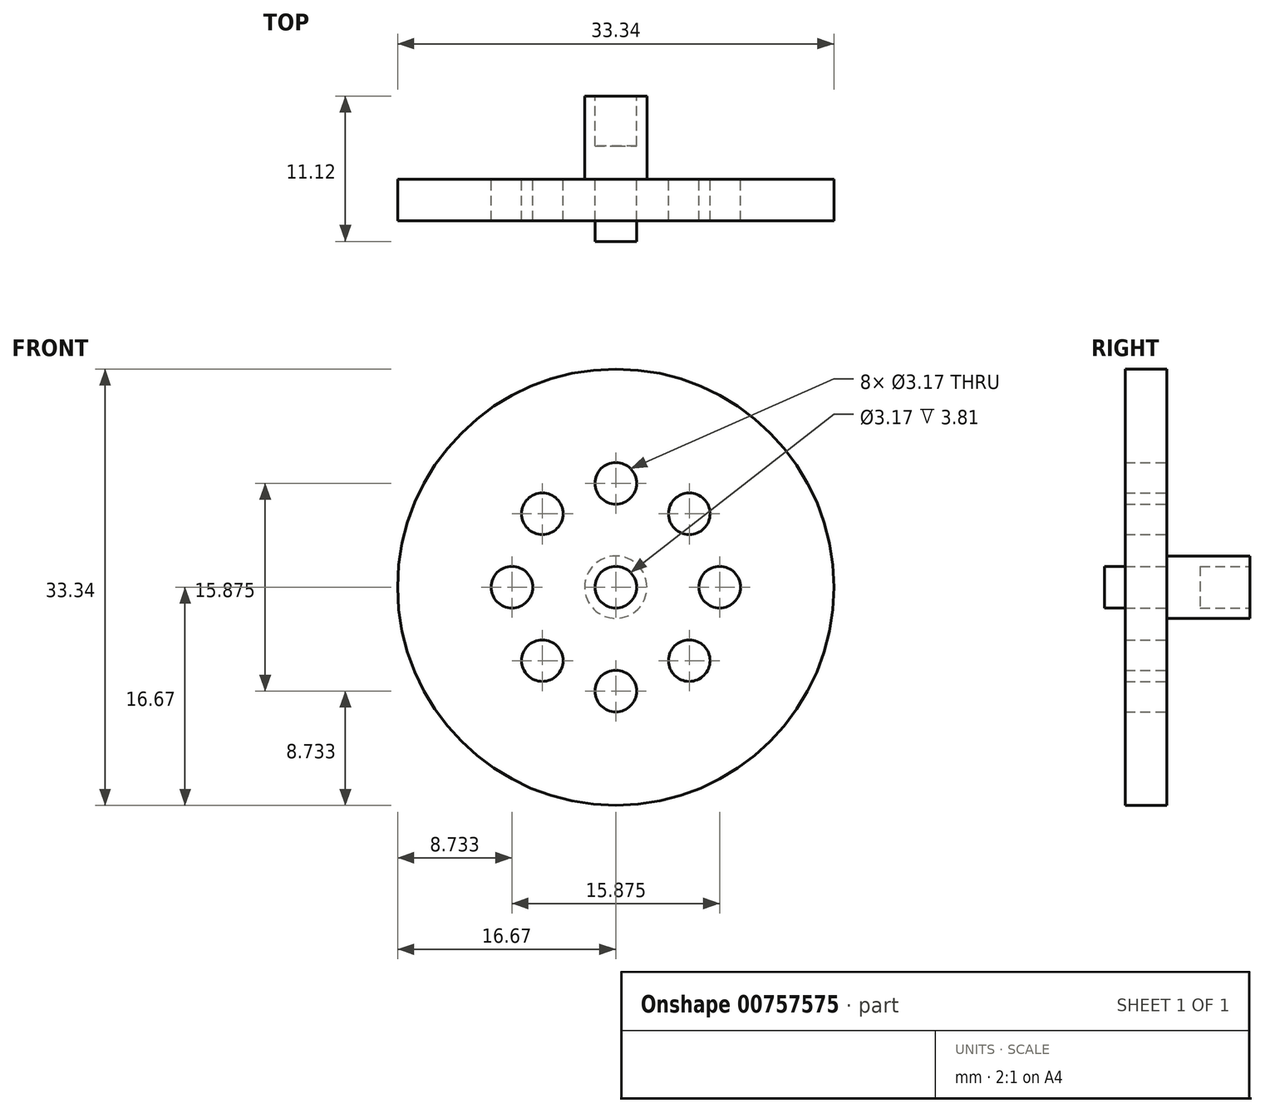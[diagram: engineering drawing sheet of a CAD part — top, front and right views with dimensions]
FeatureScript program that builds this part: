
annotation { "Feature Type Name" : "Feature", "Feature Type Description" : "" }
export const myFeature = defineFeature(function(context is Context, id is Id, definition is map)
    precondition{}
    {
        {
            var Q0;
            Q0=qCreatedBy(makeId("Front.planeOp"),FACE);
            var sketch = newSketch(context, id + "F0", { "sketchPlane" : qUnion([Q0])});
            skCircle(sketch, "E0", {"center": v(0, 0) * mm, "radius": 16.67 * mm});
            skSolve(sketch);
        }
        {
            var Q0;
            Q0=makeQuery(id+"F0.imprint","IMPRINT",FACE,{"disambiguationData":[TD([[makeQuery(id+"F0.imprint","IMPRINT",EDGE,{"derivedFrom":sQuery(id+"F0.wireOp",EDGE,"E0")}),1.0]])]});
            extrude(context, id + "F1", {"entities" : qUnion([Q0]), "oppositeDirection" : true, "depth" : 3.17 * mm, "offsetDistance" : 25.4 * mm});
        }
        {
            var Q0;
            Q0=makeQuery(id+"F1.opExtrude","CAP_FACE",FACE,{"disambiguationData":[OSD([sQuery(id+"F0.wireOp",EDGE,"E0")])],"isStart":false});
            var sketch = newSketch(context, id + "F2", { "sketchPlane" : qUnion([Q0])});
            skCircle(sketch, "E1", {"center": v(0, 0) * mm, "radius": 2.38 * mm});
            skSolve(sketch);
        }
        {
            var Q0;
            Q0=makeQuery(id+"F2.imprint","IMPRINT",FACE,{"disambiguationData":[TD([[makeQuery(id+"F2.imprint","IMPRINT",EDGE,{"derivedFrom":sQuery(id+"F2.wireOp",EDGE,"E1")}),1.0]])]});
            extrude(context, id + "F3", {"entities" : qUnion([Q0]), "operationType" : NewBodyOperationType.ADD, "depth" : 6.35 * mm, "offsetDistance" : 25.4 * mm});
        }
        {
            var Q0;
            Q0=makeQuery(id+"F3.opExtrude","CAP_FACE",FACE,{"disambiguationData":[OSD([sQuery(id+"F2.wireOp",EDGE,"E1")])],"isStart":false});
            var sketch = newSketch(context, id + "F4", { "sketchPlane" : qUnion([Q0])});
            skCircle(sketch, "E2", {"center": v(7.94, 0) * mm, "radius": 1.59 * mm});
            skCircle(sketch, "E3.1.0", {"center": v(5.61, 5.61) * mm, "radius": 1.59 * mm});
            skCircle(sketch, "E3.2.0", {"center": v(0, 7.94) * mm, "radius": 1.59 * mm});
            skCircle(sketch, "E3.3.0", {"center": v(-5.61, 5.61) * mm, "radius": 1.59 * mm});
            skCircle(sketch, "E3.4.0", {"center": v(-7.94, 0) * mm, "radius": 1.59 * mm});
            skCircle(sketch, "E3.5.0", {"center": v(-5.61, -5.61) * mm, "radius": 1.59 * mm});
            skCircle(sketch, "E3.6.0", {"center": v(0, -7.94) * mm, "radius": 1.59 * mm});
            skCircle(sketch, "E3.7.0", {"center": v(5.61, -5.61) * mm, "radius": 1.59 * mm});
            skPoint(sketch, "E3.center", {"position": v(0, 0) * mm});
            skSolve(sketch);
        }
        {
            var Q0;
            Q0 = qSketchRegion(id + "F4", true);
            extrude(context, id + "F5", {"entities" : qUnion([Q0]), "operationType" : NewBodyOperationType.REMOVE, "oppositeDirection" : true, "depth" : 25.4 * mm, "offsetDistance" : 25.4 * mm});
        }
        {
            var Q0;
            Q0=makeQuery(id+"F1.opExtrude","CAP_FACE",FACE,{"disambiguationData":[OSD([sQuery(id+"F0.wireOp",EDGE,"E0")])],"isStart":true});
            var sketch = newSketch(context, id + "F6", { "sketchPlane" : qUnion([Q0])});
            skCircle(sketch, "E4", {"center": v(0, 0) * mm, "radius": 5.56 * mm});
            skCircle(sketch, "E5", {"center": v(0, 0) * mm, "radius": 1.59 * mm});
            skSolve(sketch);
        }
        {
            var Q0;
            Q0=makeQuery(id+"F6.imprint","IMPRINT",FACE,{"disambiguationData":[TD([[makeQuery(id+"F6.imprint","IMPRINT",EDGE,{"derivedFrom":sQuery(id+"F6.wireOp",EDGE,"E5")}),1.0]])]});
            extrude(context, id + "F7", {"entities" : qUnion([Q0]), "operationType" : NewBodyOperationType.ADD, "depth" : 1.59 * mm, "offsetDistance" : 25.4 * mm});
        }
        {
            var Q0;
            Q0=makeQuery(id+"F3.opExtrude","CAP_FACE",FACE,{"disambiguationData":[OSD([sQuery(id+"F2.wireOp",EDGE,"E1")])],"isStart":false});
            var sketch = newSketch(context, id + "F8", { "sketchPlane" : qUnion([Q0])});
            skCircle(sketch, "E6", {"center": v(0, 0) * mm, "radius": 1.59 * mm});
            skSolve(sketch);
        }
        {
            var Q0;
            Q0=makeQuery(id+"F8.imprint","IMPRINT",FACE,{"disambiguationData":[TD([[makeQuery(id+"F8.imprint","IMPRINT",EDGE,{"derivedFrom":sQuery(id+"F8.wireOp",EDGE,"E6")}),1.0]])]});
            extrude(context, id + "F9", {"entities" : qUnion([Q0]), "operationType" : NewBodyOperationType.REMOVE, "oppositeDirection" : true, "depth" : 3.8 * mm, "offsetDistance" : 25.4 * mm});
        }
    });
